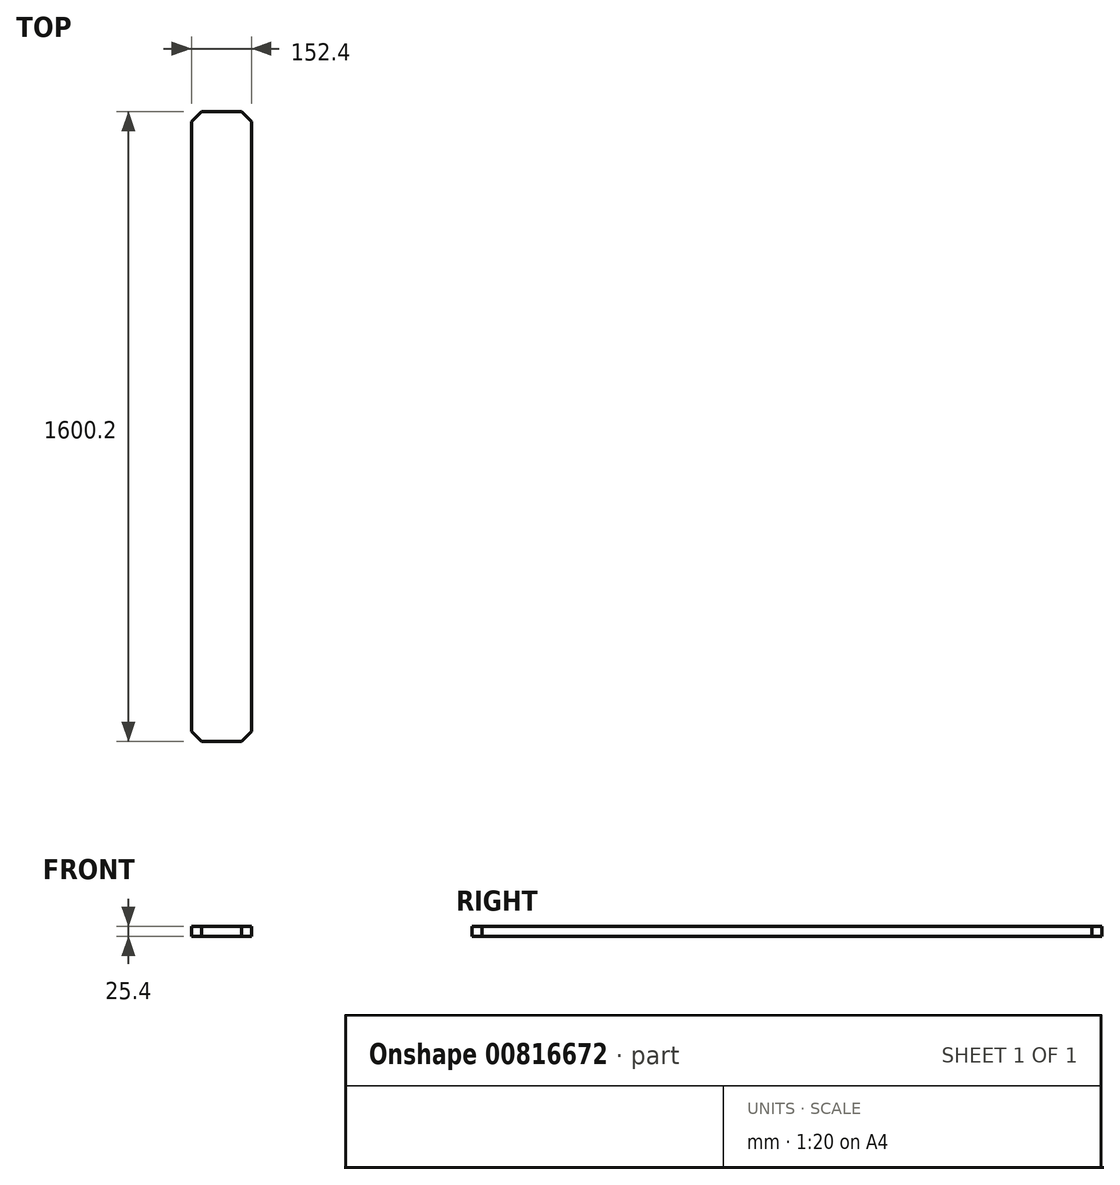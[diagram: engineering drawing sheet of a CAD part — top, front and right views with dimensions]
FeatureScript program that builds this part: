
annotation { "Feature Type Name" : "Feature", "Feature Type Description" : "" }
export const myFeature = defineFeature(function(context is Context, id is Id, definition is map)
    precondition{}
    {
        {
            var Q0;
            Q0=qCreatedBy(makeId("Top.planeOp"),FACE);
            var sketch = newSketch(context, id + "F0", { "sketchPlane" : qUnion([Q0])});
            skLineSegment(sketch, "E0.bottom", {"start": v(-282.96, -709.32) * mm, "end": v(-130.56, -709.32) * mm});
            skLineSegment(sketch, "E0.top", {"start": v(-282.96, 890.88) * mm, "end": v(-130.56, 890.88) * mm});
            skLineSegment(sketch, "E0.left", {"start": v(-282.96, -709.32) * mm, "end": v(-282.96, 890.88) * mm});
            skLineSegment(sketch, "E0.right", {"start": v(-130.56, -709.32) * mm, "end": v(-130.56, 890.88) * mm});
            skLineSegment(sketch, "E1.top", {"start": v(-282.96, -683.92) * mm, "end": v(-130.56, -683.92) * mm});
            skLineSegment(sketch, "E1.left", {"start": v(-282.96, -709.32) * mm, "end": v(-282.96, -683.92) * mm});
            skLineSegment(sketch, "E1.right", {"start": v(-130.56, -709.32) * mm, "end": v(-130.56, -683.92) * mm});
            skLineSegment(sketch, "E2.top", {"start": v(-282.96, 865.48) * mm, "end": v(-130.56, 865.48) * mm});
            skLineSegment(sketch, "E2.left", {"start": v(-282.96, 890.88) * mm, "end": v(-282.96, 865.48) * mm});
            skLineSegment(sketch, "E2.right", {"start": v(-130.56, 890.88) * mm, "end": v(-130.56, 865.48) * mm});
            skSolve(sketch);
        }
        {
            var Q0;
            {var subQ0=sQuery(id+"F0.wireOp",EDGE,"E1.top");Q0=makeQuery(id+"F0.imprint","IMPRINT",FACE,{"disambiguationData":[TD([[makeQuery(id+"F0.imprint","IMPRINT",EDGE,{"derivedFrom":subQ0}),1.0]])]});}
            var Q1;
            {var subQ0=sQuery(id+"F0.wireOp",EDGE,"E0.bottom");Q1=makeQuery(id+"F0.imprint","IMPRINT",FACE,{"disambiguationData":[TD([[makeQuery(id+"F0.imprint","IMPRINT",EDGE,{"derivedFrom":subQ0}),1.0]])]});}
            var Q2;
            {var subQ0=sQuery(id+"F0.wireOp",EDGE,"E0.top");Q2=makeQuery(id+"F0.imprint","IMPRINT",FACE,{"disambiguationData":[TD([[makeQuery(id+"F0.imprint","IMPRINT",EDGE,{"derivedFrom":subQ0}),-1.0]])]});}
            extrude(context, id + "F1", {"entities" : qUnion([Q0, Q1, Q2]), "depth" : 25.4 * mm, "offsetDistance" : 25.4 * mm});
        }
        {
            var Q0;
            Q0=makeQuery(id+"F1.opExtrude","SWEPT_EDGE",EDGE,{"disambiguationData":[OSD([sQuery(id+"F0.wireOp",EDGE,"E0.bottom"),sQuery(id+"F0.wireOp",EDGE,"E0.right")])]});
            var Q1;
            Q1=makeQuery(id+"F1.opExtrude","SWEPT_EDGE",EDGE,{"disambiguationData":[OSD([sQuery(id+"F0.wireOp",EDGE,"E0.bottom"),sQuery(id+"F0.wireOp",EDGE,"E0.left")])]});
            var Q2;
            Q2=makeQuery(id+"F1.opExtrude","SWEPT_EDGE",EDGE,{"disambiguationData":[OSD([sQuery(id+"F0.wireOp",EDGE,"E0.top"),sQuery(id+"F0.wireOp",EDGE,"E0.right")])]});
            var Q3;
            Q3=makeQuery(id+"F1.opExtrude","SWEPT_EDGE",EDGE,{"disambiguationData":[OSD([sQuery(id+"F0.wireOp",EDGE,"E0.top"),sQuery(id+"F0.wireOp",EDGE,"E0.left")])]});
            chamfer(context, id + "F2", {"entities" : qUnion([Q0, Q1, Q2, Q3]), "width" : 25.4 * mm, "tangentPropagation" : true});
        }
    });
